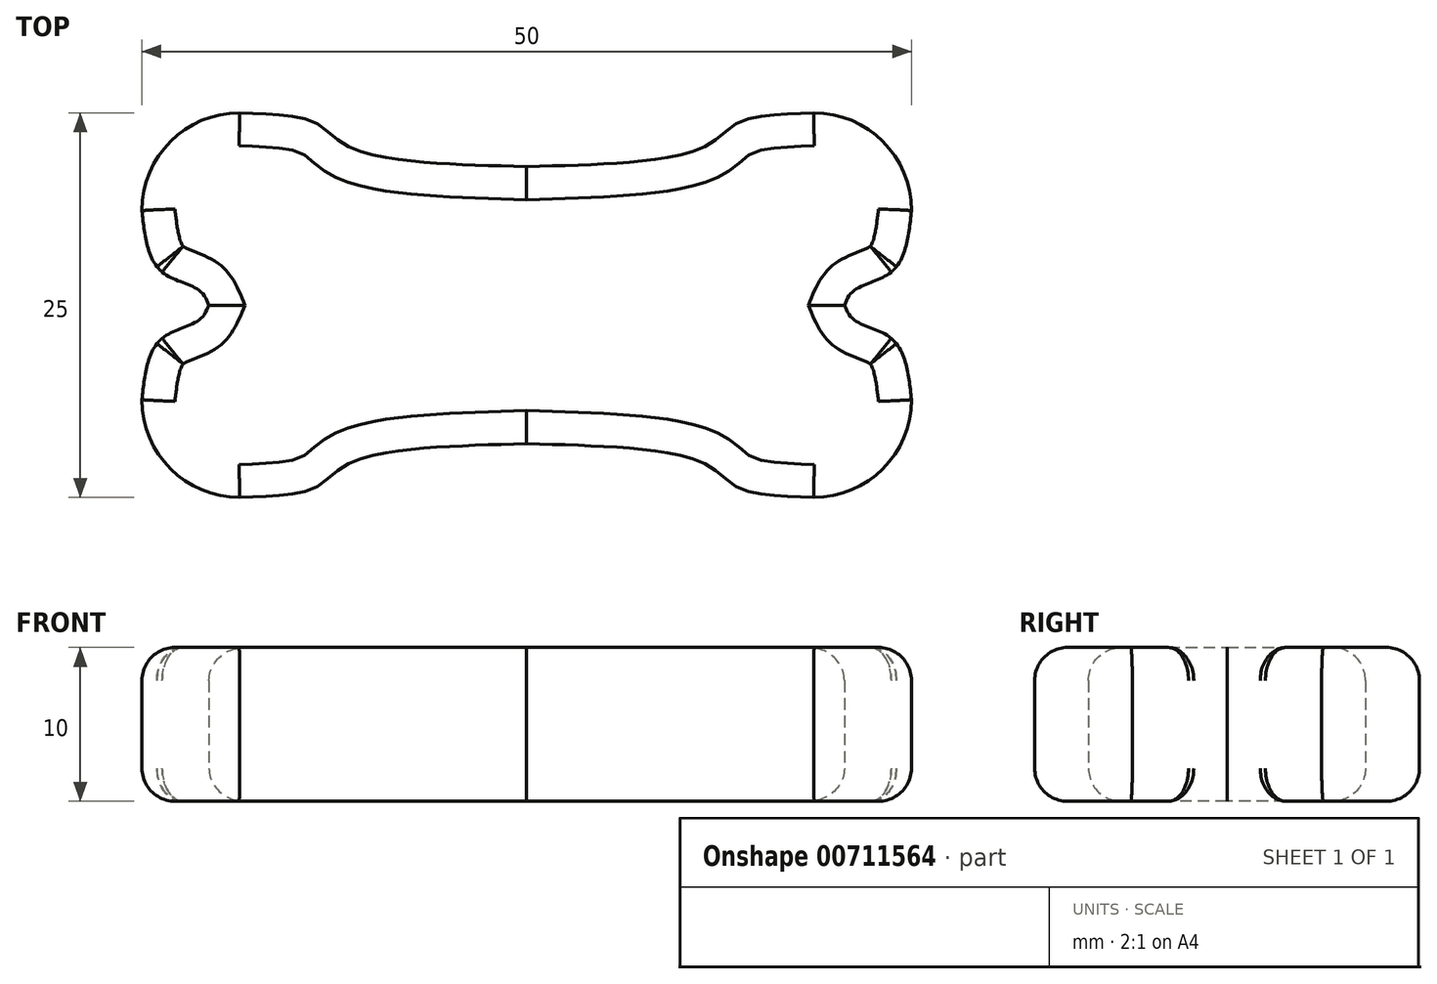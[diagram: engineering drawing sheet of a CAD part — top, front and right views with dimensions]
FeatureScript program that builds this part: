
annotation { "Feature Type Name" : "Feature", "Feature Type Description" : "" }
export const myFeature = defineFeature(function(context is Context, id is Id, definition is map)
    precondition{}
    {
        {
            var Q0;
            Q0=qCreatedBy(makeId("Top.planeOp"),FACE);
            var sketch = newSketch(context, id + "F0", { "sketchPlane" : qUnion([Q0])});
            skPoint(sketch, "E0.middle", {"position": v(0, 0) * mm});
            skPoint(sketch, "E1.visualSharp", {"position": v(-25, 12.5) * mm});
            skArc(sketch, "E1.filletArc", {"start": v(-18.65, 12.5) * mm, "mid": v(-23.14, 10.64) * mm, "end": v(-25, 6.15) * mm});
            skLineSegment(sketch, "E2", {"start": v(-25, 0) * mm, "end": v(0, 0) * mm, "construction": true});
            skLineSegment(sketch, "E3", {"start": v(0, 0) * mm, "end": v(0, 12.5) * mm});
            skFitSpline(sketch, "E4", {"points": [v(-25, 6.15) * mm, v(-23.82, 2.28) * mm, v(-21.36, 1.02) * mm, v(-20.64, 0) * mm], "startDerivative": vector(1.2, -10.93) * mm, "endDerivative": vector(2.02, -4.8) * mm});
            skFitSpline(sketch, "E5", {"points": [v(-18.65, 12.5) * mm, v(-13.68, 11.82) * mm, v(-11.52, 10.26) * mm, v(0, 9) * mm], "startDerivative": vector(18.83, -0.57) * mm, "endDerivative": vector(30.34, -0.85) * mm});
            skFitSpline(sketch, "E6.MirrorCS", {"points": [v(25, 6.15) * mm, v(23.82, 2.28) * mm, v(21.36, 1.02) * mm, v(20.64, 0) * mm], "startDerivative": vector(-1.2, -10.93) * mm, "endDerivative": vector(-2.02, -4.8) * mm});
            skArc(sketch, "E7.MirrorCS", {"start": v(18.65, 12.5) * mm, "mid": v(23.14, 10.64) * mm, "end": v(25, 6.15) * mm});
            skLineSegment(sketch, "E8.MirrorCS", {"start": v(0, 0) * mm, "end": v(0, 12.5) * mm, "construction": true});
            skLineSegment(sketch, "E9.MirrorCS", {"start": v(25, 0) * mm, "end": v(0, 0) * mm, "construction": true});
            skPoint(sketch, "E10.MirrorP", {"position": v(25, 12.5) * mm});
            skFitSpline(sketch, "E11.MirrorCS", {"points": [v(18.65, 12.5) * mm, v(13.68, 11.82) * mm, v(11.52, 10.26) * mm, v(0, 9) * mm], "startDerivative": vector(-18.83, -0.57) * mm, "endDerivative": vector(-30.34, -0.85) * mm});
            skFitSpline(sketch, "E12.MirrorCS", {"points": [v(25, -6.15) * mm, v(23.82, -2.28) * mm, v(21.36, -1.02) * mm, v(20.64, 0) * mm], "startDerivative": vector(-1.2, 10.93) * mm, "endDerivative": vector(-2.02, 4.8) * mm});
            skFitSpline(sketch, "E13.MirrorCS", {"points": [v(-25, -6.15) * mm, v(-23.82, -2.28) * mm, v(-21.36, -1.02) * mm, v(-20.64, 0) * mm], "startDerivative": vector(1.2, 10.93) * mm, "endDerivative": vector(2.02, 4.8) * mm});
            skLineSegment(sketch, "E14.MirrorCS", {"start": v(0, 0) * mm, "end": v(0, -12.5) * mm});
            skPoint(sketch, "E15.MirrorP", {"position": v(25, -12.5) * mm});
            skFitSpline(sketch, "E16.MirrorCS", {"points": [v(18.65, -12.5) * mm, v(13.68, -11.82) * mm, v(11.52, -10.26) * mm, v(0, -9) * mm], "startDerivative": vector(-18.83, 0.57) * mm, "endDerivative": vector(-30.34, 0.85) * mm});
            skLineSegment(sketch, "E17.MirrorCS", {"start": v(25, 0) * mm, "end": v(0, 0) * mm});
            skLineSegment(sketch, "E18.MirrorCS", {"start": v(-25, 0) * mm, "end": v(0, 0) * mm});
            skLineSegment(sketch, "E19.MirrorCS", {"start": v(0, 0) * mm, "end": v(0, -12.5) * mm, "construction": true});
            skArc(sketch, "E20.MirrorCS", {"start": v(18.65, -12.5) * mm, "mid": v(23.14, -10.64) * mm, "end": v(25, -6.15) * mm});
            skFitSpline(sketch, "E21.MirrorCS", {"points": [v(-18.65, -12.5) * mm, v(-13.68, -11.82) * mm, v(-11.52, -10.26) * mm, v(0, -9) * mm], "startDerivative": vector(18.83, 0.57) * mm, "endDerivative": vector(30.34, 0.85) * mm});
            skPoint(sketch, "E22.MirrorP", {"position": v(-25, -12.5) * mm});
            skArc(sketch, "E23.MirrorCS", {"start": v(-18.65, -12.5) * mm, "mid": v(-23.14, -10.64) * mm, "end": v(-25, -6.15) * mm});
            skSolve(sketch);
        }
        {
            var Q0;
            {var subQ3=sQuery(id+"F0.wireOp",EDGE,"E13.MirrorCS");Q0=makeQuery(id+"F0.imprint","IMPRINT",FACE,{"disambiguationData":[TD([[makeQuery(id+"F0.imprint","IMPRINT",EDGE,{"derivedFrom":subQ3}),-1.0]])]});}
            var Q1;
            Q1=makeQuery(id+"F0.imprint","IMPRINT",FACE,{"disambiguationData":[TD([[makeQuery(id+"F0.imprint","IMPRINT",EDGE,{"derivedFrom":sQuery(id+"F0.wireOp",EDGE,"E1.filletArc")}),1.0]])]});
            var Q2;
            {var subQ0=sQuery(id+"F0.wireOp",EDGE,"E6.MirrorCS");Q2=makeQuery(id+"F0.imprint","IMPRINT",FACE,{"disambiguationData":[TD([[makeQuery(id+"F0.imprint","IMPRINT",EDGE,{"derivedFrom":subQ0}),-1.0]])]});}
            var Q3;
            {var subQ3=sQuery(id+"F0.wireOp",EDGE,"E12.MirrorCS");Q3=makeQuery(id+"F0.imprint","IMPRINT",FACE,{"disambiguationData":[TD([[makeQuery(id+"F0.imprint","IMPRINT",EDGE,{"derivedFrom":subQ3}),1.0]])]});}
            extrude(context, id + "F1", {"entities" : qUnion([Q0, Q1, Q2, Q3]), "depth" : 5 * mm, "offsetDistance" : 25.4 * mm, "hasSecondDirection" : true, "secondDirectionOppositeDirection" : true, "secondDirectionDepth" : 5 * mm});
        }
        {
            var Q0;
            Q0=makeQuery(id+"F1.opExtrude","CAP_FACE",FACE,{"disambiguationData":[OSD([sQuery(id+"F0.wireOp",EDGE,"E1.filletArc"),sQuery(id+"F0.wireOp",EDGE,"E4"),sQuery(id+"F0.wireOp",EDGE,"E5"),sQuery(id+"F0.wireOp",EDGE,"E6.MirrorCS"),sQuery(id+"F0.wireOp",EDGE,"E7.MirrorCS"),sQuery(id+"F0.wireOp",EDGE,"E11.MirrorCS"),sQuery(id+"F0.wireOp",EDGE,"E12.MirrorCS"),sQuery(id+"F0.wireOp",EDGE,"E13.MirrorCS"),sQuery(id+"F0.wireOp",EDGE,"E16.MirrorCS"),sQuery(id+"F0.wireOp",EDGE,"E20.MirrorCS"),sQuery(id+"F0.wireOp",EDGE,"E21.MirrorCS"),sQuery(id+"F0.wireOp",EDGE,"E23.MirrorCS")])],"isStart":false});
            var Q1;
            Q1=makeQuery(id+"F1.opExtrude","CAP_FACE",FACE,{"disambiguationData":[OSD([sQuery(id+"F0.wireOp",EDGE,"E1.filletArc"),sQuery(id+"F0.wireOp",EDGE,"E4"),sQuery(id+"F0.wireOp",EDGE,"E5"),sQuery(id+"F0.wireOp",EDGE,"E6.MirrorCS"),sQuery(id+"F0.wireOp",EDGE,"E7.MirrorCS"),sQuery(id+"F0.wireOp",EDGE,"E11.MirrorCS"),sQuery(id+"F0.wireOp",EDGE,"E12.MirrorCS"),sQuery(id+"F0.wireOp",EDGE,"E13.MirrorCS"),sQuery(id+"F0.wireOp",EDGE,"E16.MirrorCS"),sQuery(id+"F0.wireOp",EDGE,"E20.MirrorCS"),sQuery(id+"F0.wireOp",EDGE,"E21.MirrorCS"),sQuery(id+"F0.wireOp",EDGE,"E23.MirrorCS")])],"isStart":true});
            fillet(context, id + "F2", {"entities" : qUnion([Q0, Q1]), "radius" : 2.15 * mm, "tangentPropagation" : true, "allowEdgeOverflow" : false});
        }
    });
